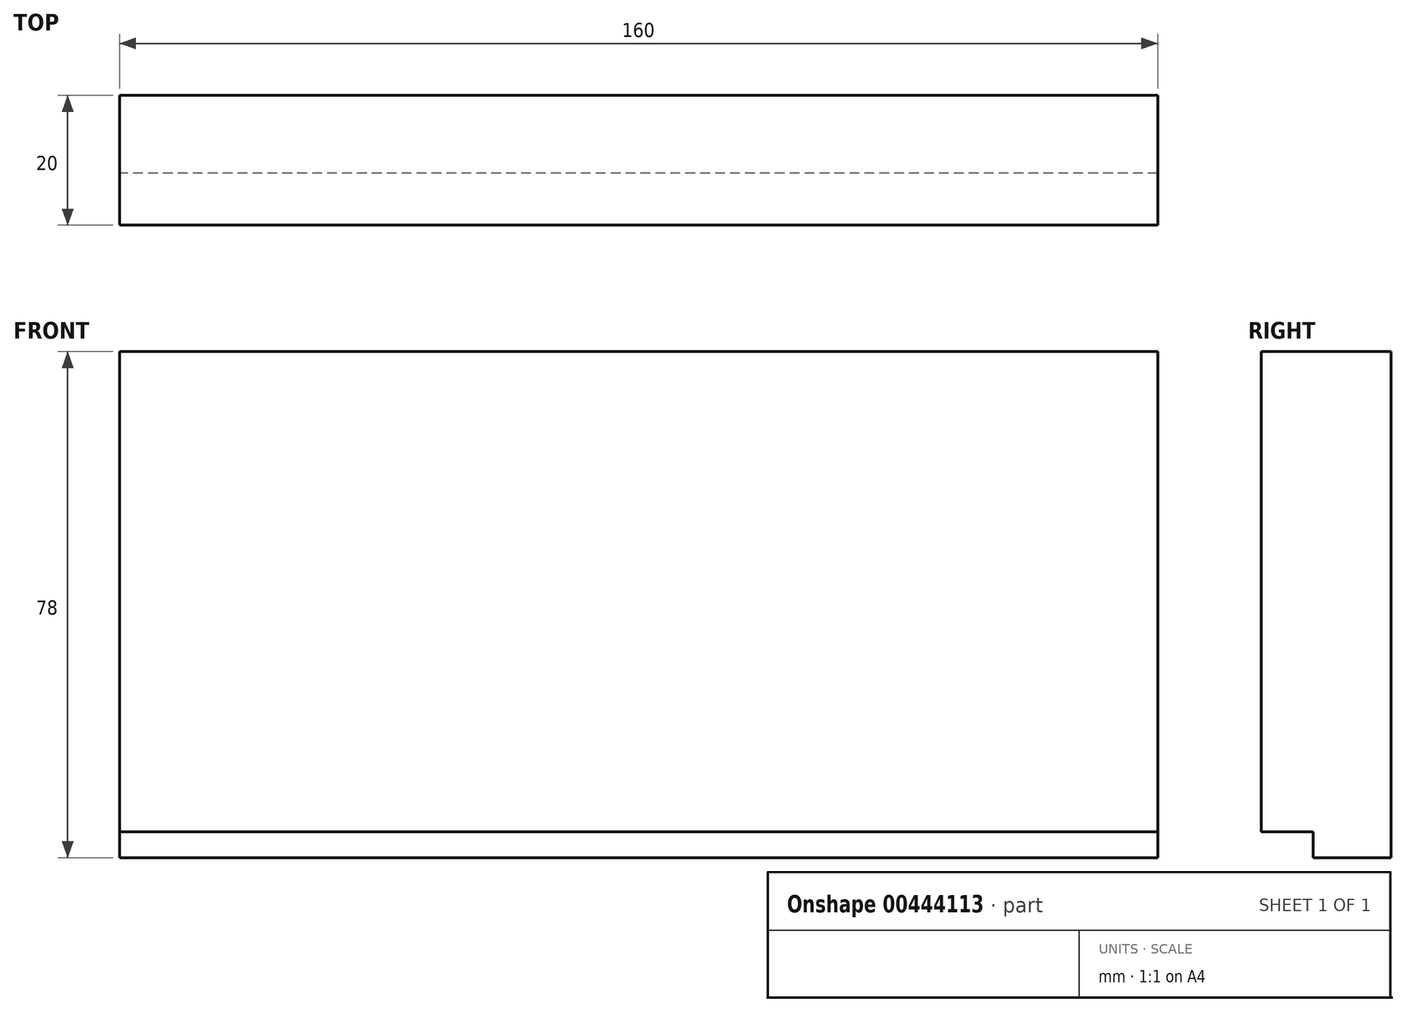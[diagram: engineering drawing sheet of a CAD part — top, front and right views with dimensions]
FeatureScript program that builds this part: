
annotation { "Feature Type Name" : "Feature", "Feature Type Description" : "" }
export const myFeature = defineFeature(function(context is Context, id is Id, definition is map)
    precondition{}
    {
        {
            var Q0;
            Q0=qCreatedBy(makeId("Right.planeOp"),FACE);
            var sketch = newSketch(context, id + "F0", { "sketchPlane" : qUnion([Q0])});
            skLineSegment(sketch, "E0", {"start": v(-41.85, 49.28) * mm, "end": v(-21.85, 49.28) * mm});
            skLineSegment(sketch, "E1", {"start": v(-21.85, 49.28) * mm, "end": v(-21.85, -28.72) * mm});
            skLineSegment(sketch, "E2", {"start": v(-21.85, -28.72) * mm, "end": v(-33.85, -28.72) * mm});
            skLineSegment(sketch, "E3", {"start": v(-33.85, -28.72) * mm, "end": v(-33.85, -24.72) * mm});
            skLineSegment(sketch, "E4", {"start": v(-33.85, -24.72) * mm, "end": v(-41.85, -24.72) * mm});
            skLineSegment(sketch, "E5", {"start": v(-41.85, 49.28) * mm, "end": v(-41.85, -24.72) * mm});
            skSolve(sketch);
        }
        {
            var Q0;
            Q0=makeQuery(id+"F0.imprint","IMPRINT",FACE,{"disambiguationData":[TD([[makeQuery(id+"F0.imprint","IMPRINT",EDGE,{"derivedFrom":sQuery(id+"F0.wireOp",EDGE,"E0")}),-1.0]])]});
            extrude(context, id + "F1", {"entities" : qUnion([Q0]), "depth" : 160 * mm});
        }
    });
